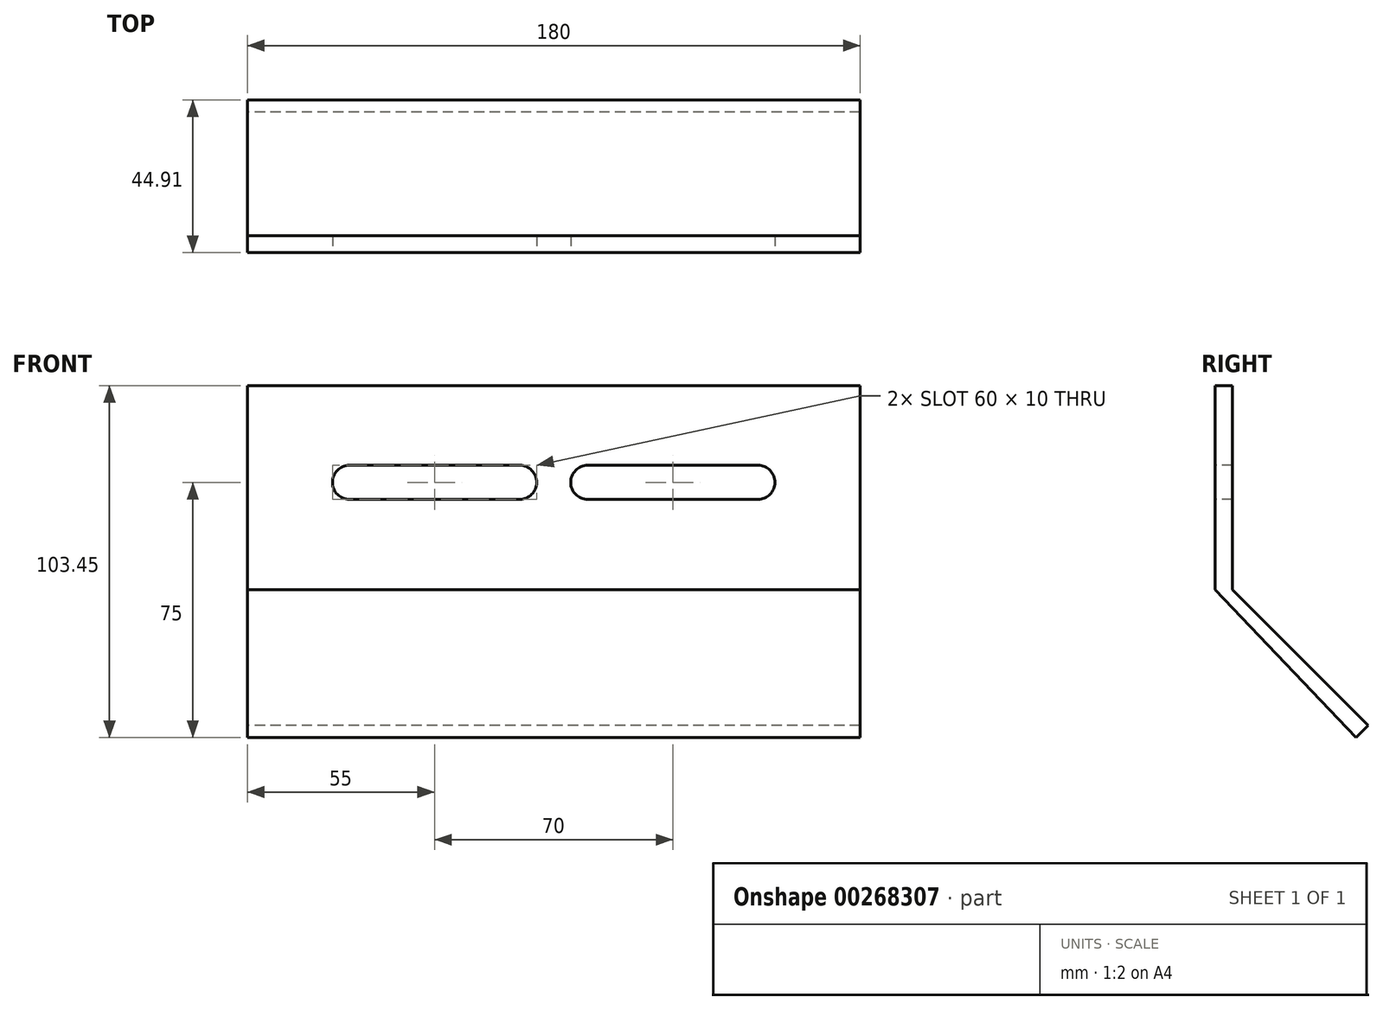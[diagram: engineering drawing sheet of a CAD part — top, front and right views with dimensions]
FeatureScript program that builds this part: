
annotation { "Feature Type Name" : "Feature", "Feature Type Description" : "" }
export const myFeature = defineFeature(function(context is Context, id is Id, definition is map)
    precondition{}
    {
        {
            var Q0;
            Q0=qCreatedBy(makeId("Front.planeOp"),FACE);
            var sketch = newSketch(context, id + "F0", { "sketchPlane" : qUnion([Q0])});
            skLineSegment(sketch, "E0.bottom", {"start": v(0, 0) * mm, "end": v(180, 0) * mm});
            skLineSegment(sketch, "E0.top", {"start": v(0, 100) * mm, "end": v(180, 100) * mm});
            skLineSegment(sketch, "E0.left", {"start": v(0, 0) * mm, "end": v(0, 100) * mm});
            skLineSegment(sketch, "E0.right", {"start": v(180, 0) * mm, "end": v(180, 100) * mm});
            skLineSegment(sketch, "E1.bottom", {"start": v(30, 80) * mm, "end": v(80, 80) * mm});
            skLineSegment(sketch, "E1.top", {"start": v(30, 70) * mm, "end": v(80, 70) * mm});
            skLineSegment(sketch, "E1.left", {"start": v(30, 80) * mm, "end": v(30, 70) * mm});
            skLineSegment(sketch, "E1.right", {"start": v(80, 80) * mm, "end": v(80, 70) * mm});
            skLineSegment(sketch, "E2.bottom", {"start": v(100, 80) * mm, "end": v(150, 80) * mm});
            skLineSegment(sketch, "E2.top", {"start": v(100, 70) * mm, "end": v(150, 70) * mm});
            skLineSegment(sketch, "E2.left", {"start": v(100, 80) * mm, "end": v(100, 70) * mm});
            skLineSegment(sketch, "E2.right", {"start": v(150, 80) * mm, "end": v(150, 70) * mm});
            skArc(sketch, "E3", {"start": v(30, 80) * mm, "mid": v(25, 75) * mm, "end": v(30, 70) * mm});
            skArc(sketch, "E4", {"start": v(100, 80) * mm, "mid": v(95, 75) * mm, "end": v(100, 70) * mm});
            skArc(sketch, "E5", {"start": v(80, 70) * mm, "mid": v(85, 75) * mm, "end": v(80, 80) * mm});
            skArc(sketch, "E6", {"start": v(150, 70) * mm, "mid": v(155, 75) * mm, "end": v(150, 80) * mm});
            skSolve(sketch);
        }
        {
            var Q0;
            Q0=qCreatedBy(makeId("Right.planeOp"),FACE);
            var sketch = newSketch(context, id + "F1", { "sketchPlane" : qUnion([Q0])});
            skLineSegment(sketch, "E7.0", {"start": v(0, 43.45) * mm, "end": v(0, 103.45) * mm});
            skLineSegment(sketch, "E8", {"start": v(0, 43.45) * mm, "end": v(41.38, 0) * mm});
            skPoint(sketch, "E9.orphan", {"position": v(0, -16.55) * mm});
            skLineSegment(sketch, "E10", {"start": v(0, 103.45) * mm, "end": v(5, 103.45) * mm});
            skLineSegment(sketch, "E11", {"start": v(5, 103.45) * mm, "end": v(5, 43.45) * mm});
            skLineSegment(sketch, "E12", {"start": v(5, 43.45) * mm, "end": v(44.91, 3.54) * mm});
            skLineSegment(sketch, "E13", {"start": v(41.38, 0) * mm, "end": v(44.91, 3.54) * mm});
            skPoint(sketch, "E14.orphan", {"position": v(48.45, 0) * mm});
            skSolve(sketch);
        }
        {
            var Q0;
            Q0 = qSketchRegion(id + "F1", true);
            extrude(context, id + "F2", {"entities" : qUnion([Q0]), "offsetDistance" : 25 * mm, "depth" : 180 * mm});
        }
        {
            var Q0;
            Q0=makeQuery(id+"F0.imprint","IMPRINT",FACE,{"disambiguationData":[TD([[makeQuery(id+"F0.imprint","IMPRINT",EDGE,{"derivedFrom":sQuery(id+"F0.wireOp",EDGE,"E1.bottom")}),-1.0]])]});
            var Q1;
            Q1=makeQuery(id+"F0.imprint","IMPRINT",FACE,{"disambiguationData":[TD([[makeQuery(id+"F0.imprint","IMPRINT",EDGE,{"derivedFrom":sQuery(id+"F0.wireOp",EDGE,"E1.right")}),1.0]])]});
            var Q2;
            Q2=makeQuery(id+"F0.imprint","IMPRINT",FACE,{"disambiguationData":[TD([[makeQuery(id+"F0.imprint","IMPRINT",EDGE,{"derivedFrom":sQuery(id+"F0.wireOp",EDGE,"E2.left")}),-1.0]])]});
            var Q3;
            Q3=makeQuery(id+"F0.imprint","IMPRINT",FACE,{"disambiguationData":[TD([[makeQuery(id+"F0.imprint","IMPRINT",EDGE,{"derivedFrom":sQuery(id+"F0.wireOp",EDGE,"E2.bottom")}),-1.0]])]});
            var Q4;
            Q4=makeQuery(id+"F0.imprint","IMPRINT",FACE,{"disambiguationData":[TD([[makeQuery(id+"F0.imprint","IMPRINT",EDGE,{"derivedFrom":sQuery(id+"F0.wireOp",EDGE,"E2.right")}),1.0]])]});
            var Q5;
            Q5=makeQuery(id+"F0.imprint","IMPRINT",FACE,{"disambiguationData":[TD([[makeQuery(id+"F0.imprint","IMPRINT",EDGE,{"derivedFrom":sQuery(id+"F0.wireOp",EDGE,"E1.left")}),-1.0]])]});
            extrude(context, id + "F3", {"entities" : qUnion([Q0, Q1, Q2, Q3, Q4, Q5]), "operationType" : NewBodyOperationType.REMOVE, "oppositeDirection" : true, "depth" : 25 * mm});
        }
    });
